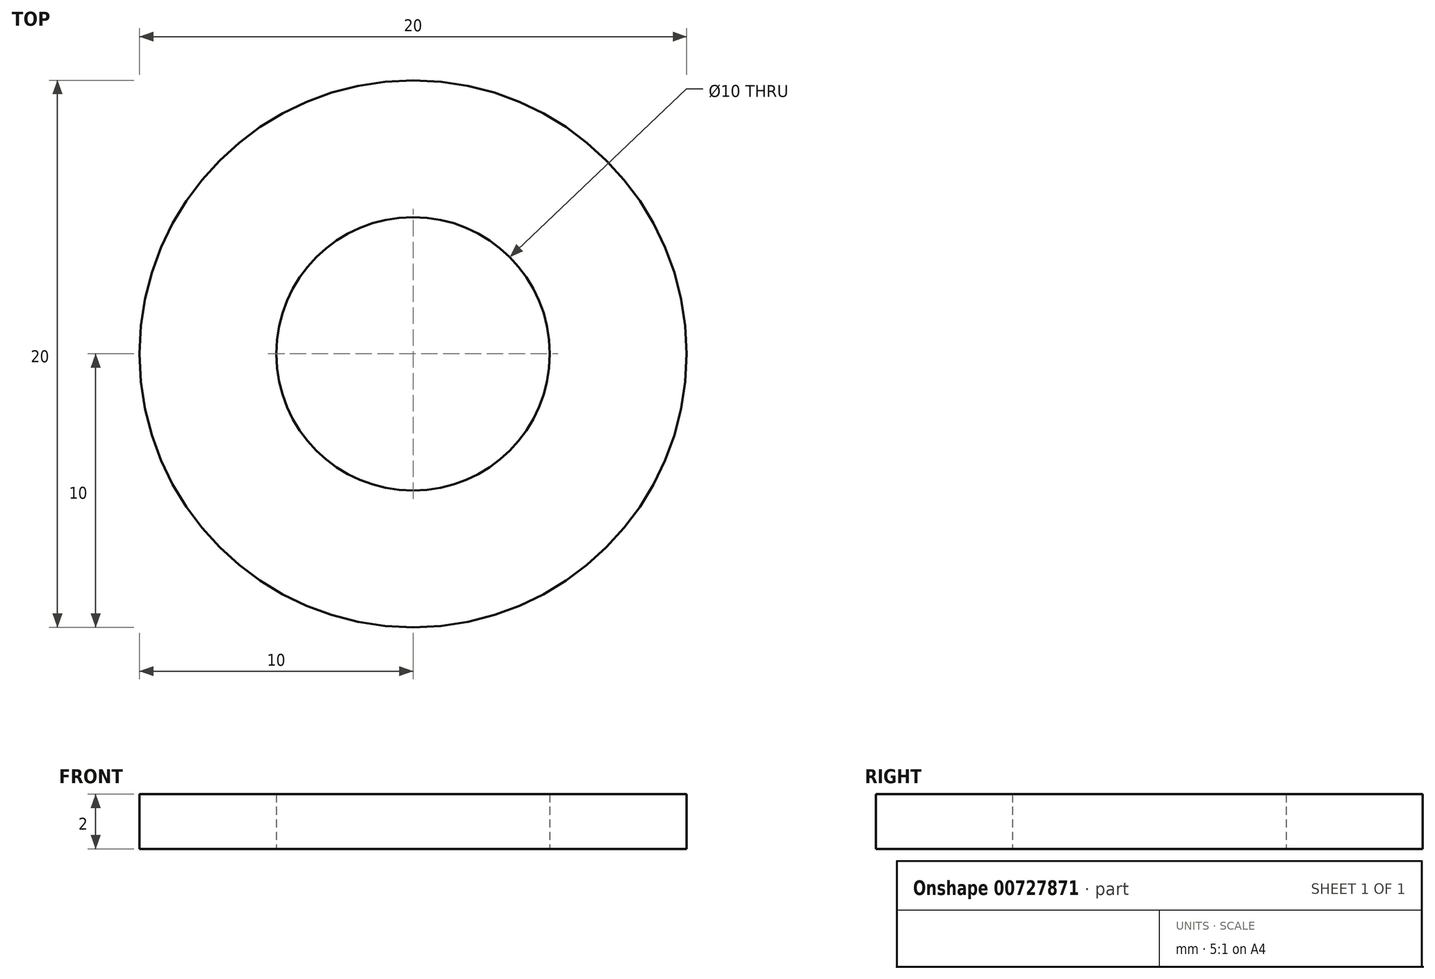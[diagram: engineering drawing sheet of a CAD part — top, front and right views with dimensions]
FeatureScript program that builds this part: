
annotation { "Feature Type Name" : "Feature", "Feature Type Description" : "" }
export const myFeature = defineFeature(function(context is Context, id is Id, definition is map)
    precondition{}
    {
        {
            var Q0;
            Q0=qCreatedBy(makeId("Top.planeOp"),FACE);
            var sketch = newSketch(context, id + "F0", { "sketchPlane" : qUnion([Q0])});
            skCircle(sketch, "E0", {"center": v(0, 0) * mm, "radius": 10 * mm});
            skCircle(sketch, "E1", {"center": v(0, 0) * mm, "radius": 5 * mm});
            skSolve(sketch);
        }
        {
            var Q0;
            Q0 = qSketchRegion(id + "F0", true);
            extrude(context, id + "F1", {"entities" : qUnion([Q0]), "depth" : 2 * mm, "offsetDistance" : 25 * mm});
        }
    });
